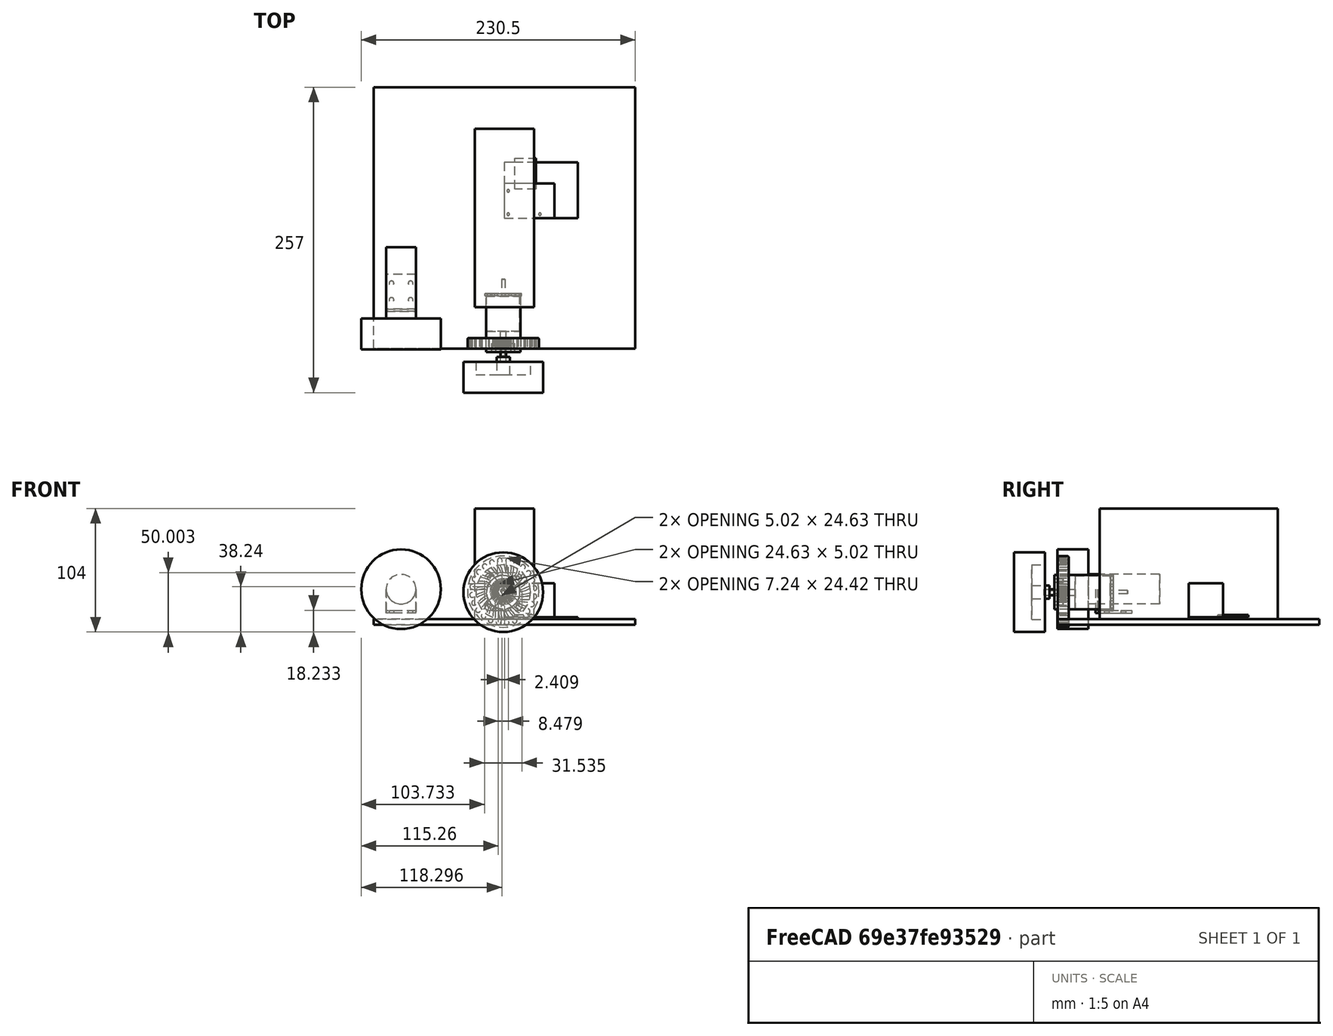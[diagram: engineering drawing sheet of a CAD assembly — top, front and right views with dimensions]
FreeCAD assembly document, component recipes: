
FREECAD ASSEMBLY — COMPONENT RECIPES ("common-components")

This assembly document has 7 components, labeled P0..P6 below (a component is one placed body or linked part). 7 of them carry a construction recipe — the FreeCAD feature program that regenerates the part from scratch, quoted from this document or its linked companion documents; the rest are supplied as boundary geometry only. No exploded tour is included for this assembly.
COMPONENT P0 — recipe-attached ("DC motor", modeled in this document).
Construction recipe (the document's own serialized feature program — sketch geometry with constraints, then the solid features built on it; lengths are millimeters unless a unit is written):

FEATURE [Sketcher::SketchObject] Sketch005
  ArcFitTolerance = 0
  AttachmentSupport = -> [YZ_Plane005]
  FullyConstrained = false
  MakeInternals = false
  MapMode = 5
  Placement = pos=(0,0,0) rot=(0.57735,0.57735,0.57735;2.0944rad)
  expr: Constraints[11] = <<dc_motor_dim>>.motor_diameter
  sketch-geometry (8):
    g0: ArcOfCircle CenterX=0 CenterY=0 CenterZ=0 NormalX=0 NormalY=0 NormalZ=1 AngleXU=0 Radius=12.5 StartAngle=0 EndAngle=3.14159
    g1: LineSegment [constr] StartX=-13.5 StartY=0 StartZ=0 EndX=13.5 EndY=0 EndZ=0
    g2: LineSegment StartX=13.5 StartY=0 StartZ=0 EndX=13.5 EndY=13.5 EndZ=0
    g3: LineSegment StartX=13.5 StartY=13.5 StartZ=0 EndX=-13.5 EndY=13.5 EndZ=0
    g4: LineSegment StartX=-13.5 StartY=13.5 StartZ=0 EndX=-13.5 EndY=0 EndZ=0
    g5: GeomPoint [constr] X=1.6e-15 Y=12.5 Z=0
    g6: LineSegment StartX=-13.5 StartY=0 StartZ=0 EndX=-12.5 EndY=1.5e-15 EndZ=0
    g7: LineSegment StartX=12.5 StartY=0 StartZ=0 EndX=13.5 EndY=0 EndZ=0
  constraints (21):
    c: Coincident(g0,g-1)
    c: PointOnObject(g0,g-1)
    c: Coincident(g1,g2)
    c: Coincident(g2,g3)
    c: Coincident(g3,g4)
    c: Coincident(g4,g1)
    c: Horizontal(g1)
    c: Horizontal(g3)
    c: Vertical(g2)
    c: Vertical(g4)
    c: PointOnObject(g5,g0)
    c: Diameter(g0) = 25
    c: PointOnObject(g2,g-1)
    c: DistanceY(g5,g2) = 1
    c: DistanceX(g0,g2) = 1
    c: DistanceX(g4,g0) = 1
    c: Coincident(g6,g4)
    c: Coincident(g7,g0)
    c: Coincident(g7,g2)
    c: Horizontal(g7)
    c: Coincident(g6,g0)
FEATURE [Sketcher::SketchObject] Sketch004
  ArcFitTolerance = 0
  AttachmentSupport = -> [XZ_Plane005]
  FullyConstrained = true
  MakeInternals = false
  MapMode = 5
  Placement = pos=(0,0,0) rot=(1,0,0;1.5708rad)
  expr: Constraints[12] = <<dc_motor_dim>>.motor_diameter / 2 + 20
  sketch-geometry (6):
    g0: LineSegment StartX=-6 StartY=12.5 StartZ=0 EndX=-6 EndY=-20 EndZ=0
    g1: LineSegment StartX=-6 StartY=-20 StartZ=0 EndX=-37 EndY=-20 EndZ=0
    g2: LineSegment StartX=-37 StartY=-20 StartZ=0 EndX=-37 EndY=-18 EndZ=0
    g3: LineSegment StartX=-37 StartY=-18 StartZ=0 EndX=-8 EndY=-18 EndZ=0
    g4: LineSegment StartX=-8 StartY=-18 StartZ=0 EndX=-8 EndY=12.5 EndZ=0
    g5: LineSegment StartX=-6 StartY=12.5 StartZ=0 EndX=-8 EndY=12.5 EndZ=0
  constraints (18):
    c: Vertical(g0)
    c: Coincident(g1,g0)
    c: Horizontal(g1)
    c: Coincident(g2,g1)
    c: Coincident(g3,g2)
    c: Horizontal(g3)
    c: Vertical(g2)
    c: Coincident(g4,g3)
    c: Vertical(g4)
    c: Distance(g2) = 2
    c: DistanceX(g0,g-1) = 6
    c: DistanceY(g0,g-1) = 20
    c: Distance(g0) = 32.5
    c: Coincident(g5,g0)
    c: Horizontal(g5)
    c: Coincident(g4,g5)
    c: DistanceX(g4,g-1) = 8
    c: Distance(g1) = 31
FEATURE [Sketcher::SketchObject] Sketch003
  ArcFitTolerance = 0
  AttachmentSupport = -> [YZ_Plane005]
  FullyConstrained = true
  MakeInternals = false
  MapMode = 5
  Placement = pos=(0,0,0) rot=(0.57735,0.57735,0.57735;2.0944rad)
  expr: Constraints[1] = <<dc_motor_dim>>.motor_diameter
  sketch-geometry (1):
    g0: Circle CenterX=0 CenterY=0 CenterZ=0 NormalX=0 NormalY=0 NormalZ=1 AngleXU=0 Radius=12.5
  constraints (2):
    c: Coincident(g0,g-1)
    c: Diameter(g0) = 25
FEATURE [Sketcher::SketchObject] Sketch002
  ArcFitTolerance = 0
  AttachmentSupport = -> [YZ_Plane005]
  FullyConstrained = true
  MakeInternals = false
  MapMode = 5
  Placement = pos=(0,0,0) rot=(0.57735,0.57735,0.57735;2.0944rad)
  expr: Constraints[1] = <<dc_motor_dim>>.wheel_diameter
  sketch-geometry (1):
    g0: Circle CenterX=0 CenterY=0 CenterZ=0 NormalX=0 NormalY=0 NormalZ=1 AngleXU=0 Radius=33.5
  constraints (2):
    c: Coincident(g0,g-1)
    c: Diameter(g0) = 67
FEATURE [PartDesign::Pad] Pad002
  Direction = (1,0,0)
  Length = 26
  Length2 = 10
  Placement = pos=(0,0,0) rot=(0.57735,0.57735,0.57735;2.0944rad)
  Profile = -> Sketch002
  ReferenceAxis = -> Sketch002 [N_Axis]
  Suppressed = false
  Type = 0
  expr: Length = <<dc_motor_dim>>.wheel_width
FEATURE [PartDesign::Pad] Pad003
  BaseFeature = -> Pad002
  Direction = (1,0,0)
  Length = 60
  Length2 = 10
  Placement = pos=(0,0,0) rot=(0.57735,0.57735,0.57735;2.0944rad)
  Profile = -> Sketch003
  ReferenceAxis = -> Sketch003 [N_Axis]
  Reversed = true
  Suppressed = false
  Type = 0
  expr: Length = <<dc_motor_dim>>.motor_length
FEATURE [PartDesign::Pad] Pad004
  BaseFeature = -> Pad003
  Direction = (0,-1,2e-16)
  Length = 25
  Length2 = 10
  Midplane = true
  Placement = pos=(0,0,0) rot=(0.57735,0.57735,0.57735;2.0944rad)
  Profile = -> Sketch004
  ReferenceAxis = -> Sketch004 [N_Axis]
  Suppressed = false
  Type = 0
  expr: Length = <<dc_motor_dim>>.motor_diameter
FEATURE [PartDesign::Pocket] Pocket
  BaseFeature = -> Pad004
  Direction = (-1,0,0)
  Length = 10
  Length2 = 5
  Placement = pos=(0,0,0) rot=(0.57735,0.57735,0.57735;2.0944rad)
  Profile = -> Sketch005
  ReferenceAxis = -> Sketch005 [N_Axis]
  Suppressed = false
  Type = 0
FEATURE [Sketcher::SketchObject] Sketch024
  ArcFitTolerance = 0
  AttachmentSupport = -> [Pocket]
  FullyConstrained = true
  MakeInternals = false
  MapMode = 5
  Placement = pos=(0,-8.8e-15,-20) rot=(0.707107,0.707107,0;3.14159rad)
  expr: Constraints[13] = <<dc_motor_dim>>.bracket_hole_diameter
  expr: Constraints[14] = <<dc_motor_dim>>.bracket_hole_width
  expr: Constraints[15] = <<dc_motor_dim>>.bracket_hole_length
  expr: Constraints[27] = <<dc_motor_dim>>.bracket_length / 2 + <<dc_motor_dim>>.bracket_thickness - 2.5
  sketch-geometry (12):
    g0: Circle CenterX=8 CenterY=-15.5 CenterZ=0 NormalX=0 NormalY=0 NormalZ=1 AngleXU=0 Radius=2
    g1: Circle CenterX=-8 CenterY=-15.5 CenterZ=0 NormalX=0 NormalY=0 NormalZ=1 AngleXU=0 Radius=2
    g2: Circle CenterX=-8 CenterY=-29.5 CenterZ=0 NormalX=0 NormalY=0 NormalZ=1 AngleXU=0 Radius=2
    g3: Circle CenterX=8 CenterY=-29.5 CenterZ=0 NormalX=0 NormalY=0 NormalZ=1 AngleXU=0 Radius=2
    g4: LineSegment [constr] StartX=-8 StartY=-15.5 StartZ=0 EndX=-8 EndY=-29.5 EndZ=0
    g5: LineSegment [constr] StartX=-8 StartY=-29.5 StartZ=0 EndX=8 EndY=-29.5 EndZ=0
    g6: LineSegment [constr] StartX=-8 StartY=-15.5 StartZ=0 EndX=8 EndY=-15.5 EndZ=0
    g7: GeomPoint [constr] X=0 Y=-15.5 Z=0
    g8: LineSegment [constr] StartX=0 StartY=-15.5 StartZ=0 EndX=0 EndY=-8 EndZ=0
    g9: LineSegment [constr] StartX=0 StartY=-8 StartZ=0 EndX=0 EndY=0 EndZ=0
    g10: LineSegment [constr] StartX=0 StartY=-15.5 StartZ=0 EndX=0 EndY=-29.5 EndZ=0
    g11: GeomPoint [constr] X=0 Y=-22.5 Z=0
  constraints (28):
    c: Equal(g1,g0)
    c: Equal(g0,g2)
    c: Equal(g2,g3)
    c: Coincident(g4,g1)
    c: Coincident(g4,g2)
    c: Coincident(g5,g2)
    c: Coincident(g5,g3)
    c: Coincident(g6,g1)
    c: Coincident(g6,g0)
    c: Horizontal(g6)
    c: Vertical(g4)
    c: Horizontal(g5)
    c: Equal(g6,g5)
    c: Diameter(g1) = 4
    c: Distance(g6) = 16
    c: Distance(g4) = 14
    c: Symmetric(g6,g6,g7)
    c: PointOnObject(g7,g-2)
    c: Coincident(g8,g7)
    c: Coincident(g9,g-1)
    c: Coincident(g8,g9)
    c: Vertical(g9)
    c: Distance(g9) = 8
    c: Coincident(g10,g7)
    c: PointOnObject(g10,g5)
    c: Vertical(g10)
    c: Symmetric(g10,g10,g11)
    c: DistanceY(g11,g8) = 14.5
FEATURE [PartDesign::Pocket] Pocket007
  BaseFeature = -> Pocket
  Direction = (0,0,1)
  Length = 2
  Length2 = 5
  Placement = pos=(0,0,0) rot=(0.57735,0.57735,0.57735;2.0944rad)
  Profile = -> Sketch024
  ReferenceAxis = -> Sketch024 [N_Axis]
  Suppressed = false
  Type = 0
  expr: Length = <<dc_motor_dim>>.bracket_thickness
FEATURE [PartDesign::Body] Body002  label="DC Motor 1"
  AllowCompound = false
  Group = -> [Sketch002,Pad002,Sketch003,Pad003,Sketch004,Pad004,Sketch005,Pocket,Sketch024,Pocket007]
  Origin = -> Origin005
  Placement = pos=(-87,-84.5,25) rot=(0,0,1;4.71239rad)
  Tip = -> Pocket007
COMPONENT P1 — recipe-attached ("Battery", modeled in this document).
Construction recipe (the document's own serialized feature program — sketch geometry with constraints, then the solid features built on it; lengths are millimeters unless a unit is written):

FEATURE [Sketcher::SketchObject] Sketch001
  ArcFitTolerance = 0
  AttachmentSupport = -> [XY_Plane004]
  FullyConstrained = false
  MakeInternals = false
  MapMode = 5
  expr: Constraints[14] = <<battery_dim>>.length
  expr: Constraints[15] = <<battery_dim>>.width
  sketch-geometry (8):
    g0: LineSegment StartX=-25 StartY=75 StartZ=0 EndX=25 EndY=75 EndZ=0
    g1: LineSegment StartX=25 StartY=75 StartZ=0 EndX=25 EndY=-75 EndZ=0
    g2: LineSegment StartX=25 StartY=-75 StartZ=0 EndX=-25 EndY=-75 EndZ=0
    g3: LineSegment StartX=-25 StartY=-75 StartZ=0 EndX=-25 EndY=75 EndZ=0
    g4: LineSegment [constr] StartX=-25 StartY=-1e-16 StartZ=0 EndX=25 EndY=-1e-16 EndZ=0
    g5: GeomPoint [constr] X=-0.40862 Y=1.74876 Z=0
    g6: GeomPoint [constr] X=0 Y=75 Z=0
    g7: GeomPoint [constr] X=0 Y=-75 Z=0
  constraints (16):
    c: Coincident(g0,g1)
    c: Coincident(g1,g2)
    c: Coincident(g2,g3)
    c: Coincident(g3,g0)
    c: Horizontal(g0)
    c: Horizontal(g2)
    c: Vertical(g1)
    c: Vertical(g3)
    c: PointOnObject(g4,g1)
    c: Horizontal(g4)
    c: Symmetric(g0,g0,g6)
    c: Symmetric(g2,g1,g7)
    c: Symmetric(g7,g6,g-1)
    c: Symmetric(g0,g2,g4)
    c: Distance(g3) = 150
    c: Distance(g2) = 50
FEATURE [PartDesign::Pad] Pad001
  Direction = (0,0,1)
  Length = 93
  Length2 = 10
  Profile = -> Sketch001
  ReferenceAxis = -> Sketch001 [N_Axis]
  Suppressed = false
  Type = 0
  expr: Length = <<battery_dim>>.height
FEATURE [PartDesign::Body] Body001  label="Battery V1"
  AllowCompound = false
  Group = -> [Sketch001,Pad001]
  Origin = -> Origin004
  Tip = -> Pad001
COMPONENT P2 — recipe-attached ("Ender3 buildplate", modeled in this document).
Construction recipe (the document's own serialized feature program — sketch geometry with constraints, then the solid features built on it; lengths are millimeters unless a unit is written):

FEATURE [Sketcher::SketchObject] Sketch016
  ArcFitTolerance = 0
  AttachmentSupport = -> [XY_Plane010]
  FullyConstrained = true
  MakeInternals = false
  MapMode = 5
  expr: Constraints[11] = <<ender3_dim>>.width
  expr: Constraints[12] = <<ender3_dim>>.height
  sketch-geometry (6):
    g0: LineSegment StartX=-110 StartY=110 StartZ=0 EndX=110 EndY=110 EndZ=0
    g1: LineSegment StartX=110 StartY=110 StartZ=0 EndX=110 EndY=-110 EndZ=0
    g2: LineSegment StartX=110 StartY=-110 StartZ=0 EndX=-110 EndY=-110 EndZ=0
    g3: LineSegment StartX=-110 StartY=-110 StartZ=0 EndX=-110 EndY=110 EndZ=0
    g4: GeomPoint [constr] X=2.7e-15 Y=-110 Z=0
    g5: GeomPoint [constr] X=-2.7e-15 Y=110 Z=0
  constraints (13):
    c: Coincident(g0,g1)
    c: Coincident(g1,g2)
    c: Coincident(g2,g3)
    c: Coincident(g3,g0)
    c: Horizontal(g0)
    c: Horizontal(g2)
    c: Vertical(g1)
    c: Vertical(g3)
    c: Symmetric(g0,g0,g5)
    c: Symmetric(g2,g1,g4)
    c: Symmetric(g4,g5,g-1)
    c: Distance(g0) = 220
    c: Distance(g1) = 220
FEATURE [PartDesign::Pad] Pad013
  Direction = (0,0,1)
  Length = 5
  Length2 = 10
  Profile = -> Sketch016
  ReferenceAxis = -> Sketch016 [N_Axis]
  Reversed = true
  Suppressed = false
  Type = 0
FEATURE [PartDesign::Body] Body005  label="plate"
  AllowCompound = false
  Group = -> [Sketch016,Pad013]
  Origin = -> Origin010
  Tip = -> Pad013
COMPONENT P3 — recipe-attached ("PCB", modeled in this document).
Construction recipe (the document's own serialized feature program — sketch geometry with constraints, then the solid features built on it; lengths are millimeters unless a unit is written):

FEATURE [Sketcher::SketchObject] Sketch022
  ArcFitTolerance = 0
  AttachmentSupport = -> [XY_Plane012]
  FullyConstrained = true
  MakeInternals = false
  MapMode = 5
  sketch-geometry (7):
    g0: LineSegment StartX=0 StartY=0 StartZ=0 EndX=61.6 EndY=0 EndZ=0
    g1: LineSegment StartX=61.6 StartY=0 StartZ=0 EndX=61.6 EndY=47 EndZ=0
    g2: LineSegment StartX=61.6 StartY=47 StartZ=0 EndX=0 EndY=47 EndZ=0
    g3: LineSegment StartX=0 StartY=47 StartZ=0 EndX=0 EndY=0 EndZ=0
    g4: Circle CenterX=3.175 CenterY=3.175 CenterZ=0 NormalX=0 NormalY=0 NormalZ=1 AngleXU=0 Radius=1.1
    g5: Circle CenterX=3.175 CenterY=22.86 CenterZ=0 NormalX=0 NormalY=0 NormalZ=1 AngleXU=0 Radius=1.1
    g6: Circle CenterX=29.845 CenterY=3.175 CenterZ=0 NormalX=0 NormalY=0 NormalZ=1 AngleXU=0 Radius=1.1
  constraints (20):
    c: Coincident(g0,g1)
    c: Coincident(g1,g2)
    c: Coincident(g2,g3)
    c: Coincident(g3,g0)
    c: Horizontal(g0)
    c: Horizontal(g2)
    c: Vertical(g1)
    c: Vertical(g3)
    c: Coincident(g0,g-1)
    c: Distance(g0) = 61.6
    c: Distance(g1) = 47
    c: Equal(g6,g4)
    c: Equal(g4,g5)
    c: Diameter(g4) = 2.2
    c: DistanceX(g0,g4) = 3.175
    c: DistanceX(g4,g5) = 0
    c: DistanceY(g0,g4) = 3.175
    c: DistanceY(g4,g6) = 0
    c: DistanceY(g0,g5) = 22.86
    c: DistanceX(g0,g6) = 29.845
FEATURE [PartDesign::Pad] Pad015
  Direction = (0,0,1)
  Length = 1.6
  Length2 = 10
  Profile = -> Sketch022
  ReferenceAxis = -> Sketch022 [N_Axis]
  Suppressed = false
  Type = 0
FEATURE [PartDesign::Body] Body006  label="PCB plate"
  AllowCompound = false
  Group = -> [Sketch022,Pad015]
  Origin = -> Origin012
  Tip = -> Pad015
FEATURE [Sketcher::SketchObject] Sketch023
  ArcFitTolerance = 0
  AttachmentSupport = -> [Pad015]
  FullyConstrained = true
  MakeInternals = false
  MapMode = 5
  Placement = pos=(0,0,1.6) rot=(0,0,1;0rad)
  expr: Constraints[10] = 3.21 + 47
  sketch-geometry (4):
    g0: LineSegment StartX=8.6 StartY=50.21 StartZ=0 EndX=26.6 EndY=50.21 EndZ=0
    g1: LineSegment StartX=26.6 StartY=50.21 StartZ=0 EndX=26.6 EndY=24.465 EndZ=0
    g2: LineSegment StartX=26.6 StartY=24.465 StartZ=0 EndX=8.6 EndY=24.465 EndZ=0
    g3: LineSegment StartX=8.6 StartY=24.465 StartZ=0 EndX=8.6 EndY=50.21 EndZ=0
  constraints (12):
    c: Coincident(g0,g1)
    c: Coincident(g1,g2)
    c: Coincident(g2,g3)
    c: Coincident(g3,g0)
    c: Horizontal(g0)
    c: Horizontal(g2)
    c: Vertical(g1)
    c: Vertical(g3)
    c: Distance(g0) = 18
    c: DistanceX(g-1,g2) = 8.6
    c: DistanceY(g-1,g0) = 50.21
    c: Distance(g3) = 25.745
FEATURE [PartDesign::Pad] Pad016
  Direction = (0,0,1)
  Length = 1.6
  Length2 = 10
  Profile = -> Sketch023
  ReferenceAxis = -> Sketch023 [N_Axis]
  Suppressed = false
  Type = 0
FEATURE [PartDesign::Body] Body007  label="ESP32 module"
  AllowCompound = false
  Group = -> [Sketch023,Pad016]
  Origin = -> Origin013
  Tip = -> Pad016
COMPONENT P4 — recipe-attached ("BL motor car", modeled in this document).
Construction recipe (the document's own serialized feature program — sketch geometry with constraints, then the solid features built on it; lengths are millimeters unless a unit is written):

FEATURE [PartDesign::Plane] DatumPlane002
  AttachmentOffset = pos=(0,0,-8) rot=(0,0,1;0rad)
  AttachmentSupport = -> [XZ_Plane016]
  Length = 80.3208
  MapMode = 5
  Placement = pos=(0,8,-1.8e-15) rot=(1,0,0;1.5708rad)
  ResizeMode = 0
  Width = 80.3553
FEATURE [Sketcher::SketchObject] Sketch036
  ArcFitTolerance = 0
  AttachmentSupport = -> [DatumPlane002]
  FullyConstrained = true
  MakeInternals = false
  MapMode = 5
  Placement = pos=(0,8,-1.8e-15) rot=(1,0,0;1.5708rad)
  sketch-geometry (2):
    g0: Circle CenterX=0 CenterY=0 CenterZ=0 NormalX=0 NormalY=0 NormalZ=1 AngleXU=0 Radius=23
    g1: Circle CenterX=0 CenterY=0 CenterZ=0 NormalX=0 NormalY=0 NormalZ=1 AngleXU=0 Radius=5.5
  constraints (4):
    c: Coincident(g0,g-1)
    c: Diameter(g0) = 46
    c: Coincident(g1,g0)
    c: Diameter(g1) = 11
FEATURE [Sketcher::SketchObject] Sketch035
  ArcFitTolerance = 0
  AttachmentSupport = -> [XZ_Plane016]
  FullyConstrained = true
  MakeInternals = false
  MapMode = 5
  Placement = pos=(0,0,0) rot=(1,0,0;1.5708rad)
  expr: Constraints[15] = <<bl_motor_dim>>.bracket_screw_diameter
  expr: Constraints[16] = <<bl_motor_dim>>.bracket_hole_width
  expr: Constraints[17] = <<bl_motor_dim>>.bracket_hole_length
  sketch-geometry (8):
    g0: Circle CenterX=-1.994e-13 CenterY=-9.5 CenterZ=0 NormalX=0 NormalY=0 NormalZ=1 AngleXU=0 Radius=1.5
    g1: Circle CenterX=8 CenterY=0 CenterZ=0 NormalX=0 NormalY=0 NormalZ=1 AngleXU=0 Radius=1.5
    g2: Circle CenterX=0 CenterY=9.5 CenterZ=0 NormalX=0 NormalY=0 NormalZ=1 AngleXU=0 Radius=1.5
    g3: Circle CenterX=-8 CenterY=0 CenterZ=0 NormalX=0 NormalY=0 NormalZ=1 AngleXU=0 Radius=1.5
    g4: Circle [constr] CenterX=0 CenterY=0 CenterZ=0 NormalX=0 NormalY=0 NormalZ=1 AngleXU=0 Radius=9.5
    g5: Circle [constr] CenterX=0 CenterY=0 CenterZ=0 NormalX=0 NormalY=0 NormalZ=1 AngleXU=0 Radius=8
    g6: LineSegment [constr] StartX=-1.994e-13 StartY=-9.5 StartZ=0 EndX=0 EndY=9.5 EndZ=0
    g7: LineSegment [constr] StartX=-8 StartY=0 StartZ=0 EndX=8 EndY=0 EndZ=0
  constraints (20):
    c: Coincident(g4,g-1)
    c: PointOnObject(g0,g4)
    c: Coincident(g5,g4)
    c: PointOnObject(g3,g5)
    c: Coincident(g6,g0)
    c: Coincident(g6,g2)
    c: Coincident(g7,g3)
    c: Coincident(g7,g1)
    c: PointOnObject(g1,g5)
    c: PointOnObject(g2,g4)
    c: PointOnObject(g4,g6)
    c: PointOnObject(g4,g7)
    c: Equal(g1,g3)
    c: Equal(g0,g2)
    c: Equal(g0,g1)
    c: Diameter(g0) = 3
    c: Diameter(g5) = 16
    c: Diameter(g4) = 19
    c: PointOnObject(g1,g-1)
    c: PointOnObject(g2,g-2)
FEATURE [Sketcher::SketchObject] Sketch034
  ArcFitTolerance = 0
  AttachmentSupport = -> [DatumPlane002]
  FullyConstrained = true
  MakeInternals = false
  MapMode = 5
  Placement = pos=(0,8,-1.8e-15) rot=(1,0,0;1.5708rad)
  expr: Constraints[1] = <<bl_motor_dim>>.wheel_diameter
  sketch-geometry (1):
    g0: Circle CenterX=0 CenterY=0 CenterZ=0 NormalX=0 NormalY=0 NormalZ=1 AngleXU=0 Radius=33.5
  constraints (2):
    c: Coincident(g0,g-1)
    c: Diameter(g0) = 67
FEATURE [Sketcher::SketchObject] Sketch032
  ArcFitTolerance = 0
  AttachmentSupport = -> [YZ_Plane016]
  FullyConstrained = true
  MakeInternals = false
  MapMode = 5
  Placement = pos=(0,0,0) rot=(0.57735,0.57735,0.57735;2.0944rad)
  expr: Constraints[10] = 3.18 / 2
  sketch-geometry (4):
    g0: LineSegment StartX=3 StartY=1.21412 StartZ=0 EndX=15 EndY=1.21412 EndZ=0
    g1: LineSegment StartX=15 StartY=1.21412 StartZ=0 EndX=15 EndY=1.59 EndZ=0
    g2: LineSegment StartX=15 StartY=1.59 StartZ=0 EndX=2.86319 EndY=1.59 EndZ=0
    g3: LineSegment StartX=2.86319 StartY=1.59 StartZ=0 EndX=3 EndY=1.21412 EndZ=0
  constraints (12):
    c: Horizontal(g0)
    c: Coincident(g1,g0)
    c: Coincident(g2,g1)
    c: Horizontal(g2)
    c: Coincident(g3,g2)
    c: Coincident(g3,g0)
    c: DistanceX(g0,g0) = 12
    c: Distance(g3) = 0.4
    c: Angle(g0,g3) = 1.91986
    c: Vertical(g1)
    c: DistanceY(g-1,g2) = 1.59
    c: DistanceX(g-1,g0) = 15
FEATURE [Sketcher::SketchObject] Sketch031
  ArcFitTolerance = 0
  AttachmentSupport = -> [XZ_Plane016]
  FullyConstrained = true
  MakeInternals = false
  MapMode = 5
  Placement = pos=(0,0,0) rot=(1,0,0;1.5708rad)
  sketch-geometry (1):
    g0: Circle CenterX=0 CenterY=0 CenterZ=0 NormalX=0 NormalY=0 NormalZ=1 AngleXU=0 Radius=1.5875
  constraints (2):
    c: Coincident(g0,g-1)
    c: Diameter(g0) = 3.175
FEATURE [Sketcher::SketchObject] Sketch030
  ArcFitTolerance = 0
  AttachmentSupport = -> [XZ_Plane016]
  FullyConstrained = true
  MakeInternals = false
  MapMode = 5
  Placement = pos=(0,0,0) rot=(1,0,0;1.5708rad)
  expr: Constraints[1] = <<bl_motor_dim>>.motor_diameter
  sketch-geometry (1):
    g0: Circle CenterX=0 CenterY=0 CenterZ=0 NormalX=0 NormalY=0 NormalZ=1 AngleXU=0 Radius=14.5
  constraints (2):
    c: Coincident(g0,g-1)
    c: Diameter(g0) = 29
FEATURE [PartDesign::Pad] Pad018
  Direction = (0,-1,2e-16)
  Length = 47
  Length2 = 10
  Placement = pos=(0,0,0) rot=(1,0,0;1.5708rad)
  Profile = -> Sketch030
  ReferenceAxis = -> Sketch030 [N_Axis]
  Suppressed = false
  Type = 0
  expr: Length = <<bl_motor_dim>>.motor_length
FEATURE [PartDesign::Pad] Pad019
  BaseFeature = -> Pad018
  Direction = (0,-1,2e-16)
  Length = 15
  Length2 = 10
  Placement = pos=(0,0,0) rot=(1,0,0;1.5708rad)
  Profile = -> Sketch031
  ReferenceAxis = -> Sketch031 [N_Axis]
  Reversed = true
  Suppressed = false
  Type = 0
FEATURE [PartDesign::Pocket] Pocket012
  BaseFeature = -> Pad019
  Direction = (-1,0,0)
  Length = 10
  Length2 = 5
  Midplane = true
  Placement = pos=(0,0,0) rot=(1,0,0;1.5708rad)
  Profile = -> Sketch032
  ReferenceAxis = -> Sketch032 [N_Axis]
  Suppressed = false
  Type = 0
FEATURE [Sketcher::SketchObject] Sketch033
  ArcFitTolerance = 0
  AttachmentSupport = -> [Pocket012]
  FullyConstrained = true
  MakeInternals = false
  MapMode = 5
  Placement = pos=(0,15,-3.3e-15) rot=(-1,0,0;1.5708rad)
  sketch-geometry (1):
    g0: Circle CenterX=0 CenterY=0 CenterZ=0 NormalX=0 NormalY=0 NormalZ=1 AngleXU=0 Radius=5.5
  constraints (2):
    c: Coincident(g0,g-1)
    c: Diameter(g0) = 11
FEATURE [PartDesign::Pad] Pad020
  BaseFeature = -> Pocket012
  Direction = (0,1,2e-16)
  Length = 11
  Length2 = 10
  Placement = pos=(0,0,0) rot=(1,0,0;1.5708rad)
  Profile = -> Sketch033
  ReferenceAxis = -> Sketch033 [N_Axis]
  Reversed = true
  Suppressed = false
  Type = 0
FEATURE [PartDesign::Pad] Pad021
  BaseFeature = -> Pad020
  Direction = (0,-1,2e-16)
  Length = 26
  Length2 = 10
  Placement = pos=(0,0,0) rot=(1,0,0;1.5708rad)
  Profile = -> Sketch034
  ReferenceAxis = -> Sketch034 [N_Axis]
  Reversed = true
  Suppressed = false
  Type = 0
  expr: Length = <<bl_motor_dim>>.wheel_width
FEATURE [PartDesign::Pocket] Pocket013
  BaseFeature = -> Pad021
  Direction = (0,1,-2e-16)
  Length = 7.5
  Length2 = 5
  Placement = pos=(0,0,0) rot=(1,0,0;1.5708rad)
  Profile = -> Sketch035
  ReferenceAxis = -> Sketch035 [N_Axis]
  Reversed = true
  Suppressed = false
  Type = 0
FEATURE [PartDesign::Pocket] Pocket014
  BaseFeature = -> Pocket013
  Direction = (0,1,-2e-16)
  Length = 11
  Length2 = 5
  Placement = pos=(0,0,0) rot=(1,0,0;1.5708rad)
  Profile = -> Sketch036
  ReferenceAxis = -> Sketch036 [N_Axis]
  Suppressed = false
  Type = 0
FEATURE [PartDesign::Body] Body010  label="BL Motor car 1"
  AllowCompound = false
  Group = -> [Sketch030,Pad018,Sketch031,Pad019,Sketch032,Pocket012,Sketch033,Pad020,DatumPlane002,Sketch034,Pad021,Sketch035,Pocket013,Sketch036,Pocket014]
  Origin = -> Origin016
  Placement = pos=(-1,-113,22.5) rot=(0,0,1;3.14159rad)
  Tip = -> Pocket014
COMPONENT P5 — recipe-attached ("Drone motor", modeled in this document).
Construction recipe (the document's own serialized feature program — sketch geometry with constraints, then the solid features built on it; lengths are millimeters unless a unit is written):

FEATURE [Sketcher::SketchObject] Sketch052
  ArcFitTolerance = 0
  AttachmentSupport = -> [XZ_Plane022]
  FullyConstrained = false
  MakeInternals = false
  MapMode = 5
  Placement = pos=(0,0,0) rot=(1,0,0;1.5708rad)
  expr: Constraints[97] = <<drone_motor_dim>>.bracket_screw_diameter
  sketch-geometry (44):
    g0: Circle [constr] CenterX=0 CenterY=0 CenterZ=0 NormalX=0 NormalY=0 NormalZ=1 AngleXU=0 Radius=20.5
    g1: ArcOfCircle CenterX=0 CenterY=16.9985 CenterZ=0 NormalX=0 NormalY=0 NormalZ=1 AngleXU=0 Radius=3.50149 StartAngle=0.0291986 EndAngle=3.11239
    g2: ArcOfCircle CenterX=0 CenterY=-16.9985 CenterZ=0 NormalX=0 NormalY=0 NormalZ=1 AngleXU=0 Radius=3.50149 StartAngle=3.14271 EndAngle=6.25399
    g3: ArcOfCircle CenterX=-17 CenterY=0 CenterZ=0 NormalX=0 NormalY=0 NormalZ=1 AngleXU=0 Radius=3.5 StartAngle=1.5708 EndAngle=4.71239
    g4: ArcOfCircle CenterX=17 CenterY=0 CenterZ=0 NormalX=0 NormalY=0 NormalZ=1 AngleXU=0 Radius=3.5 StartAngle=4.71238 EndAngle=7.85398
    g5: GeomPoint [constr] X=20.5 Y=0 Z=0
    g6: GeomPoint [constr] X=-20.5 Y=-3.4401e-06 Z=0
    g7: GeomPoint [constr] X=-0.00272726 Y=-20.5 Z=0
    g8: GeomPoint [constr] X=-0.000240899 Y=20.5 Z=0
    g9: LineSegment [constr] StartX=-3.5 StartY=17.1007 StartZ=0 EndX=3.5 EndY=17.1007 EndZ=0
    g10: LineSegment [constr] StartX=-17 StartY=3.5 StartZ=0 EndX=-17 EndY=-3.5 EndZ=0
    g11: LineSegment StartX=-8.5 StartY=3.5 StartZ=0 EndX=-17 EndY=3.5 EndZ=0
    g12: LineSegment StartX=-3.5 StartY=17.1007 StartZ=0 EndX=-3.5 EndY=8.5 EndZ=0
    g13: LineSegment StartX=3.5 StartY=8.5 StartZ=0 EndX=3.5 EndY=17.1007 EndZ=0
    g14: LineSegment StartX=17 StartY=3.5 StartZ=0 EndX=8.5 EndY=3.5 EndZ=0
    g15: LineSegment [constr] StartX=3.5 StartY=3.5 StartZ=0 EndX=-3.5 EndY=3.5 EndZ=0
    g16: LineSegment StartX=8.5 StartY=-3.5 StartZ=0 EndX=17 EndY=-3.5 EndZ=0
    g17: LineSegment StartX=-17 StartY=-3.5 StartZ=0 EndX=-8.50149 EndY=-3.5 EndZ=0
    g18: LineSegment [constr] StartX=-3.50149 StartY=-3.5 StartZ=0 EndX=3.5 EndY=-3.5 EndZ=0
    g19: LineSegment [constr] StartX=-3.5 StartY=3.5 StartZ=0 EndX=-3.5 EndY=-3.5 EndZ=0
    g20: LineSegment StartX=-3.50149 StartY=-8.5 StartZ=0 EndX=-3.50149 EndY=-17.0024 EndZ=0
    g21: LineSegment StartX=3.5 StartY=-17.1007 StartZ=0 EndX=3.5 EndY=-8.5 EndZ=0
    g22: LineSegment [constr] StartX=3.5 StartY=-3.5 StartZ=0 EndX=3.5 EndY=3.5 EndZ=0
    g23: ArcOfCircle CenterX=-8.5 CenterY=8.5 CenterZ=0 NormalX=0 NormalY=0 NormalZ=1 AngleXU=0 Radius=5 StartAngle=4.71239 EndAngle=6.28319
    g24: ArcOfCircle CenterX=8.5 CenterY=8.5 CenterZ=0 NormalX=0 NormalY=0 NormalZ=1 AngleXU=0 Radius=5 StartAngle=3.14159 EndAngle=4.71239
    g25: ArcOfCircle CenterX=8.5 CenterY=-8.5 CenterZ=0 NormalX=0 NormalY=0 NormalZ=1 AngleXU=0 Radius=5 StartAngle=1.5708 EndAngle=3.14159
    g26: ArcOfCircle CenterX=-8.50149 CenterY=-8.5 CenterZ=0 NormalX=0 NormalY=0 NormalZ=1 AngleXU=0 Radius=5 StartAngle=0 EndAngle=1.5708
    g27: LineSegment [constr] StartX=-8.50149 StartY=-8.5 StartZ=0 EndX=-8.50149 EndY=-3.5 EndZ=0
    g28: LineSegment [constr] StartX=8.5 StartY=-8.5 StartZ=0 EndX=8.5 EndY=-3.5 EndZ=0
    g29: LineSegment [constr] StartX=8.5 StartY=3.5 StartZ=0 EndX=8.5 EndY=8.5 EndZ=0
    g30: LineSegment [constr] StartX=-8.5 StartY=3.5 StartZ=0 EndX=-8.5 EndY=8.5 EndZ=0
    g31: LineSegment [constr] StartX=-8.5 StartY=3.5 StartZ=0 EndX=-3.5 EndY=3.5 EndZ=0
    g32: LineSegment [constr] StartX=-3.5 StartY=8.5 StartZ=0 EndX=-3.5 EndY=3.5 EndZ=0
    g33: LineSegment [constr] StartX=-8.50149 StartY=-3.5 StartZ=0 EndX=-3.50149 EndY=-3.5 EndZ=0
    g34: LineSegment [constr] StartX=3.5 StartY=-3.5 StartZ=0 EndX=8.5 EndY=-3.5 EndZ=0
    g35: LineSegment [constr] StartX=3.5 StartY=3.5 StartZ=0 EndX=8.5 EndY=3.5 EndZ=0
    g36: LineSegment [constr] StartX=3.5 StartY=3.5 StartZ=0 EndX=3.5 EndY=8.5 EndZ=0
    g37: LineSegment [constr] StartX=3.5 StartY=-8.5 StartZ=0 EndX=3.5 EndY=-3.5 EndZ=0
    g38: LineSegment [constr] StartX=-3.50149 StartY=-8.5 StartZ=0 EndX=-3.50149 EndY=-3.5 EndZ=0
    g39: Circle CenterX=0 CenterY=16.9985 CenterZ=0 NormalX=0 NormalY=0 NormalZ=1 AngleXU=0 Radius=1.5
    g40: Circle CenterX=-17 CenterY=0 CenterZ=0 NormalX=0 NormalY=0 NormalZ=1 AngleXU=0 Radius=1.5
    g41: Circle CenterX=17 CenterY=0 CenterZ=0 NormalX=0 NormalY=0 NormalZ=1 AngleXU=0 Radius=1.5
    g42: Circle CenterX=0 CenterY=-16.4205 CenterZ=0 NormalX=0 NormalY=0 NormalZ=1 AngleXU=0 Radius=1.5
    g43: Circle CenterX=0 CenterY=0 CenterZ=0 NormalX=0 NormalY=0 NormalZ=1 AngleXU=0 Radius=5
  constraints (106):
    c: Coincident(g0,g-1)
    c: Diameter(g0) = 41
    c: Coincident(g1,g12) = -1.5708
    c: Coincident(g20,g2) = -1.5708
    c: Coincident(g2,g21) = -1.5708
    c: Coincident(g13,g1) = -1.5708
    c: Equal(g1,g2)
    c: PointOnObject(g1,g-2)
    c: Coincident(g3,g17) = -1.5708
    c: Coincident(g16,g4) = -1.5708
    c: Coincident(g4,g14) = -1.5708
    c: Coincident(g11,g3) = -1.5708
    c: Equal(g3,g4)
    c: PointOnObject(g3,g-1)
    c: PointOnObject(g5,g4)
    c: PointOnObject(g6,g3)
    c: PointOnObject(g7,g2)
    c: PointOnObject(g8,g1)
    c: PointOnObject(g4,g-1)
    c: PointOnObject(g2,g-2)
    c: PointOnObject(g8,g0)
    c: PointOnObject(g7,g0)
    c: PointOnObject(g5,g0)
    c: PointOnObject(g6,g0)
    c: Coincident(g9,g1)
    c: Coincident(g9,g1)
    c: Coincident(g10,g3)
    c: Coincident(g10,g3)
    c: Distance(g10) = 7
    c: Equal(g9,g10)
    c: PointOnObject(g22,g18)
    c: PointOnObject(g18,g22)
    c: PointOnObject(g19,g18)
    c: PointOnObject(g18,g20)
    c: PointOnObject(g15,g19)
    c: PointOnObject(g19,g15)
    c: PointOnObject(g22,g15)
    c: PointOnObject(g15,g22)
    c: Vertical(g13)
    c: Vertical(g12)
    c: Vertical(g20)
    c: Vertical(g21)
    c: Horizontal(g16)
    c: Horizontal(g14)
    c: Horizontal(g11)
    c: Horizontal(g17)
    c: Vertical(g10)
    c: Horizontal(g15)
    c: Horizontal(g18)
    c: PointOnObject(g5,g-1)
    c: PointOnObject(g3,g10)
    c: Tangent(g11,g23) = 1.5708
    c: Tangent(g12,g23) = 1.5708
    c: Tangent(g14,g24) = 1.5708
    c: Tangent(g13,g24) = 1.5708
    c: Tangent(g16,g25) = 1.5708
    c: Tangent(g21,g25) = 1.5708
    c: Tangent(g17,g26) = 1.5708
    c: Tangent(g20,g26) = 1.5708
    c: Coincident(g27,g26)
    c: Coincident(g27,g17)
    c: Coincident(g28,g25)
    c: Coincident(g28,g16)
    c: Coincident(g29,g14)
    c: Coincident(g29,g24)
    c: Coincident(g30,g11)
    c: Coincident(g30,g23)
    c: Distance(g27) = 5
    c: Equal(g30,g29)
    c: Equal(g29,g28)
    c: Equal(g28,g27)
    c: Coincident(g31,g11)
    c: Coincident(g31,g15)
    c: Coincident(g32,g12)
    c: Coincident(g32,g15)
    c: Coincident(g33,g17)
    c: Coincident(g33,g18)
    c: Coincident(g34,g18)
    c: Coincident(g34,g16)
    c: Tangent(g34,g25)
    c: Coincident(g35,g15)
    c: Coincident(g35,g14)
    c: Coincident(g36,g15)
    c: Coincident(g36,g13)
    c: Coincident(g37,g21)
    c: Coincident(g37,g18)
    c: Coincident(g38,g20)
    c: Coincident(g38,g18)
    c: Vertical(g22)
    c: Vertical(g37)
    c: Vertical(g32)
    c: Vertical(g19)
    c: Horizontal(g31)
    c: Vertical(g36)
    c: Horizontal(g33)
    c: Horizontal(g9)
    c: Coincident(g39,g1)
    c: Diameter(g39) = 3
    c: Coincident(g40,g3)
    c: Coincident(g41,g4)
    c: PointOnObject(g42,g-2)
    c: Equal(g42,g41)
    c: Equal(g41,g40)
    c: Equal(g40,g39)
    c: Coincident(g43,g0)
    c: Diameter(g43) = 10
FEATURE [PartDesign::Pad] Pad031  label="bracket"
  Direction = (0,-1,2e-16)
  Length = 2
  Length2 = 10
  Placement = pos=(0,0,0) rot=(1,0,0;1.5708rad)
  Profile = -> Sketch052
  ReferenceAxis = -> Sketch052 [N_Axis]
  Suppressed = false
  Type = 0
FEATURE [Sketcher::SketchObject] Sketch053
  ArcFitTolerance = 0
  AttachmentSupport = -> [Pad031]
  FullyConstrained = true
  MakeInternals = false
  MapMode = 5
  Placement = pos=(0,-2,4e-16) rot=(1,0,0;1.5708rad)
  sketch-geometry (1):
    g0: Circle CenterX=0 CenterY=0 CenterZ=0 NormalX=0 NormalY=0 NormalZ=1 AngleXU=0 Radius=14
  constraints (2):
    c: Coincident(g0,g-1)
    c: Diameter(g0) = 28
FEATURE [PartDesign::Pad] Pad032
  BaseFeature = -> Pad031
  Direction = (0,-1,2e-16)
  Length = 30
  Length2 = 10
  Placement = pos=(0,0,0) rot=(1,0,0;1.5708rad)
  Profile = -> Sketch053
  ReferenceAxis = -> Sketch053 [N_Axis]
  Suppressed = false
  Type = 0
FEATURE [Sketcher::SketchObject] Sketch054
  ArcFitTolerance = 0
  AttachmentSupport = -> [Pad032]
  FullyConstrained = true
  MakeInternals = false
  MapMode = 5
  Placement = pos=(0,-2,4e-16) rot=(-1,0,0;1.5708rad)
  sketch-geometry (1):
    g0: Circle CenterX=0 CenterY=0 CenterZ=0 NormalX=0 NormalY=0 NormalZ=1 AngleXU=0 Radius=1.5
  constraints (2):
    c: Coincident(g0,g-1)
    c: Diameter(g0) = 3
FEATURE [PartDesign::Pad] Pad033
  BaseFeature = -> Pad032
  Direction = (0,1,2e-16)
  Length = 14
  Length2 = 10
  Placement = pos=(0,0,0) rot=(1,0,0;1.5708rad)
  Profile = -> Sketch054
  ReferenceAxis = -> Sketch054 [N_Axis]
  Suppressed = false
  Type = 0
FEATURE [Sketcher::SketchObject] Sketch055
  ArcFitTolerance = 0
  AttachmentSupport = -> [Pad033]
  FullyConstrained = true
  MakeInternals = false
  MapMode = 5
  Placement = pos=(0,-32,7e-15) rot=(1,0,0;1.5708rad)
  sketch-geometry (1):
    g0: Circle CenterX=0 CenterY=0 CenterZ=0 NormalX=0 NormalY=0 NormalZ=1 AngleXU=0 Radius=2.5
  constraints (2):
    c: Coincident(g0,g-1)
    c: Diameter(g0) = 5
FEATURE [PartDesign::Pad] Pad034
  BaseFeature = -> Pad033
  Direction = (0,-1,2e-16)
  Length = 26
  Length2 = 10
  Placement = pos=(0,0,0) rot=(1,0,0;1.5708rad)
  Profile = -> Sketch055
  ReferenceAxis = -> Sketch055 [N_Axis]
  Suppressed = false
  Type = 0
FEATURE [PartDesign::Body] Body014  label="BL Motor drone 1"
  AllowCompound = false
  Group = -> [Sketch052,Pad031,Sketch053,Pad032,Sketch054,Pad033,Sketch055,Pad034]
  Origin = -> Origin022
  Placement = pos=(-1,-63.5,22.5) rot=(0,1,0;0.785398rad)
  Tip = -> Pad034
FEATURE [Sketcher::SketchObject] Sketch061
  ArcFitTolerance = 0
  AttachmentSupport = -> [XZ_Plane024]
  FullyConstrained = true
  MakeInternals = false
  MapMode = 5
  Placement = pos=(0,0,0) rot=(1,0,0;1.5708rad)
  sketch-geometry (1):
    g0: Circle CenterX=0 CenterY=0 CenterZ=0 NormalX=0 NormalY=0 NormalZ=1 AngleXU=0 Radius=2.5
  constraints (2):
    c: Coincident(g0,g-1)
    c: Diameter(g0) = 5
FEATURE [Sketcher::SketchObject] Sketch060
  ArcFitTolerance = 0
  AttachmentSupport = -> [XZ_Plane024]
  FullyConstrained = true
  MakeInternals = false
  MapMode = 5
  Placement = pos=(0,0,0) rot=(1,0,0;1.5708rad)
  expr: Constraints[13] = <<drone_motor_dim>>.wheel_diameter / 2
  expr: Constraints[3] = <<drone_motor_dim>>.wheel_diameter
  sketch-geometry (12):
    g0: Circle [constr] CenterX=0 CenterY=0 CenterZ=0 NormalX=0 NormalY=0 NormalZ=1 AngleXU=0 Radius=30
    g1: ArcOfCircle CenterX=30 CenterY=0 CenterZ=0 NormalX=0 NormalY=0 NormalZ=1 AngleXU=0 Radius=30 StartAngle=3.27249 EndAngle=4.01895
    g2: LineSegment [constr] StartX=10.8245 StartY=-23.0716 StartZ=0 EndX=8.26777 EndY=-26.1478 EndZ=0
    g3: LineSegment [constr] StartX=10.8245 StartY=-23.0716 StartZ=0 EndX=30 EndY=0 EndZ=0
    g4: LineSegment [constr] StartX=30 StartY=0 StartZ=0 EndX=0.256654 EndY=-3.91579 EndZ=0
    g5: LineSegment [constr] StartX=0.256654 StartY=-3.91579 StartZ=0 EndX=0.15751 EndY=-3.92884 EndZ=0
    g6: ArcOfCircle CenterX=9.54613 CenterY=-24.6097 CenterZ=0 NormalX=0 NormalY=0 NormalZ=1 AngleXU=0 Radius=2 StartAngle=4.01895 EndAngle=7.16055
    g7: ArcOfCircle [constr] CenterX=30 CenterY=0 CenterZ=0 NormalX=0 NormalY=0 NormalZ=1 AngleXU=0 Radius=32 StartAngle=4.01895 EndAngle=4.14985
    g8: ArcOfCircle [constr] CenterX=30 CenterY=0 CenterZ=0 NormalX=0 NormalY=0 NormalZ=1 AngleXU=0 Radius=30.1 StartAngle=3.14159 EndAngle=3.27249
    g9: LineSegment [constr] StartX=12.9333 StartY=-27.069 StartZ=0 EndX=30 EndY=0 EndZ=0
    g10: ArcOfCircle CenterX=29.4271 CenterY=-5.83469 CenterZ=0 NormalX=0 NormalY=0 NormalZ=1 AngleXU=0 Radius=29.3316 StartAngle=3.07657 EndAngle=3.90659
    g11: ArcOfCircle CenterX=0.207082 CenterY=-3.92231 CenterZ=0 NormalX=0 NormalY=0 NormalZ=1 AngleXU=0 Radius=0.05 StartAngle=0.1309 EndAngle=3.27249
  constraints (34):
    c: Coincident(g0,g-1)
    c: PointOnObject(g1,g0)
    c: PointOnObject(g1,g-1)
    c: Diameter(g0) = 60
    c: Coincident(g2,g1)
    c: Coincident(g3,g1)
    c: Coincident(g3,g1)
    c: Parallel(g3,g2)
    c: Distance(g2) = 4
    c: Coincident(g4,g1)
    c: Coincident(g4,g1)
    c: Coincident(g5,g1)
    c: Parallel(g5,g4)
    c: Distance(g4) = 30
    c: Coincident(g6,g1)
    c: Coincident(g7,g1)
    c: Coincident(g7,g6)
    c: PointOnObject(g7,g0)
    c: Coincident(g8,g1)
    c: PointOnObject(g8,g-1)
    c: Angle(g-1,g4) = 0.1309
    c: Coincident(g9,g7)
    c: Coincident(g9,g1)
    c: Angle(g3,g9) = 0.1309
    c: PointOnObject(g10,g0)
    c: Coincident(g10,g8)
    c: Coincident(g10,g6)
    c: Coincident(g2,g6)
    c: Coincident(g10,g5)
    c: Distance(g5) = 0.1
    c: PointOnObject(g6,g2)
    c: Coincident(g11,g10)
    c: Coincident(g11,g1)
    c: PointOnObject(g11,g5)
FEATURE [Sketcher::SketchObject] Sketch059
  ArcFitTolerance = 0
  AttachmentSupport = -> [XZ_Plane024]
  FullyConstrained = true
  MakeInternals = false
  MapMode = 5
  Placement = pos=(0,0,0) rot=(1,0,0;1.5708rad)
  expr: Constraints[1] = <<drone_motor_dim>>.wheel_diameter
  sketch-geometry (1):
    g0: Circle CenterX=0 CenterY=0 CenterZ=0 NormalX=0 NormalY=0 NormalZ=1 AngleXU=0 Radius=30
  constraints (2):
    c: Coincident(g0,g-1)
    c: Diameter(g0) = 60
FEATURE [PartDesign::Pad] Pad036
  Direction = (0,-1,2e-16)
  Length = 9
  Length2 = 10
  Placement = pos=(0,0,0) rot=(1,0,0;1.5708rad)
  Profile = -> Sketch059
  ReferenceAxis = -> Sketch059 [N_Axis]
  Suppressed = false
  Type = 0
  expr: Length = <<drone_motor_dim>>.wheel_width_center
FEATURE [PartDesign::Pocket] Pocket022
  BaseFeature = -> Pad036
  Direction = (0,1,-2e-16)
  Length = 100
  Length2 = 5
  Placement = pos=(0,0,0) rot=(1,0,0;1.5708rad)
  Profile = -> Sketch060
  ReferenceAxis = -> Sketch060 [N_Axis]
  Reversed = true
  Suppressed = false
  Type = 0
FEATURE [PartDesign::PolarPattern] PolarPattern
  Angle = 360
  Axis = -> Sketch060 [N_Axis]
  BaseFeature = -> Pocket022
  Mode = 0
  Occurrences = 24
  Offset = 120
  Originals = -> [Pocket022]
  Placement = pos=(0,0,0) rot=(1,0,0;1.5708rad)
  Suppressed = false
  TransformMode = 0
FEATURE [PartDesign::Pocket] Pocket023
  BaseFeature = -> PolarPattern
  Direction = (0,1,-2e-16)
  Length = 100
  Length2 = 5
  Placement = pos=(0,0,0) rot=(1,0,0;1.5708rad)
  Profile = -> Sketch061
  ReferenceAxis = -> Sketch061 [N_Axis]
  Reversed = true
  Suppressed = false
  Type = 0
FEATURE [PartDesign::Fillet] Fillet
  Base = -> Pocket023 [Edge2,Edge3]
  BaseFeature = -> Pocket023
  Placement = pos=(0,0,0) rot=(1,0,0;1.5708rad)
  Radius = 1
  SupportTransform = false
  Suppressed = false
  UseAllEdges = false
FEATURE [PartDesign::Body] Body016  label="Drone wheel 1"
  AllowCompound = false
  Group = -> [Sketch059,Pad036,Sketch060,Pocket022,PolarPattern,Sketch061,Pocket023,Fillet]
  Origin = -> Origin024
  Placement = pos=(-1,-101,23) rot=(0,0,1;0rad)
  Tip = -> Fillet
COMPONENT P6 — recipe-attached ("BL motor driver", modeled in this document).
Construction recipe (the document's own serialized feature program — sketch geometry with constraints, then the solid features built on it; lengths are millimeters unless a unit is written):

FEATURE [Sketcher::SketchObject] Sketch
  ArcFitTolerance = 1e-06
  AttachmentSupport = -> [XY_Plane028]
  FullyConstrained = true
  MakeInternals = false
  MapMode = 5
  expr: Constraints[10] = <<driver_dim>>.width
  expr: Constraints[9] = <<driver_dim>>.depth
  sketch-geometry (4):
    g0: LineSegment StartX=0 StartY=0 StartZ=0 EndX=42 EndY=0 EndZ=0
    g1: LineSegment StartX=42 StartY=0 StartZ=0 EndX=42 EndY=29 EndZ=0
    g2: LineSegment StartX=42 StartY=29 StartZ=0 EndX=0 EndY=29 EndZ=0
    g3: LineSegment StartX=0 StartY=29 StartZ=0 EndX=0 EndY=0 EndZ=0
  constraints (11):
    c: Coincident(g0,g1)
    c: Coincident(g1,g2)
    c: Coincident(g2,g3)
    c: Coincident(g3,g0)
    c: Horizontal(g0)
    c: Horizontal(g2)
    c: Vertical(g1)
    c: Vertical(g3)
    c: Coincident(g0,g-1)
    c: DistanceY(g1,g1) = 29
    c: DistanceX(g2,g2) = 42
FEATURE [PartDesign::Pad] Pad
  Direction = (0,0,1)
  Length = 30
  Length2 = 10
  Profile = -> Sketch
  ReferenceAxis = -> Sketch [N_Axis]
  Refine = true
  Suppressed = false
  Type = 0
  expr: Length = <<driver_dim>>.height
FEATURE [PartDesign::Body] Body
  AllowCompound = false
  Group = -> [Sketch,Pad]
  Origin = -> Origin028
  Tip = -> Pad
PROVENANCE & LICENSES
A FreeCAD (.FCStd) document from a public repository crawl; recipes are the document's own serialized feature recipes (and, for linked parts, companion documents' recipes).
License: as declared in the source repository (recorded in the dataset sidecar).
